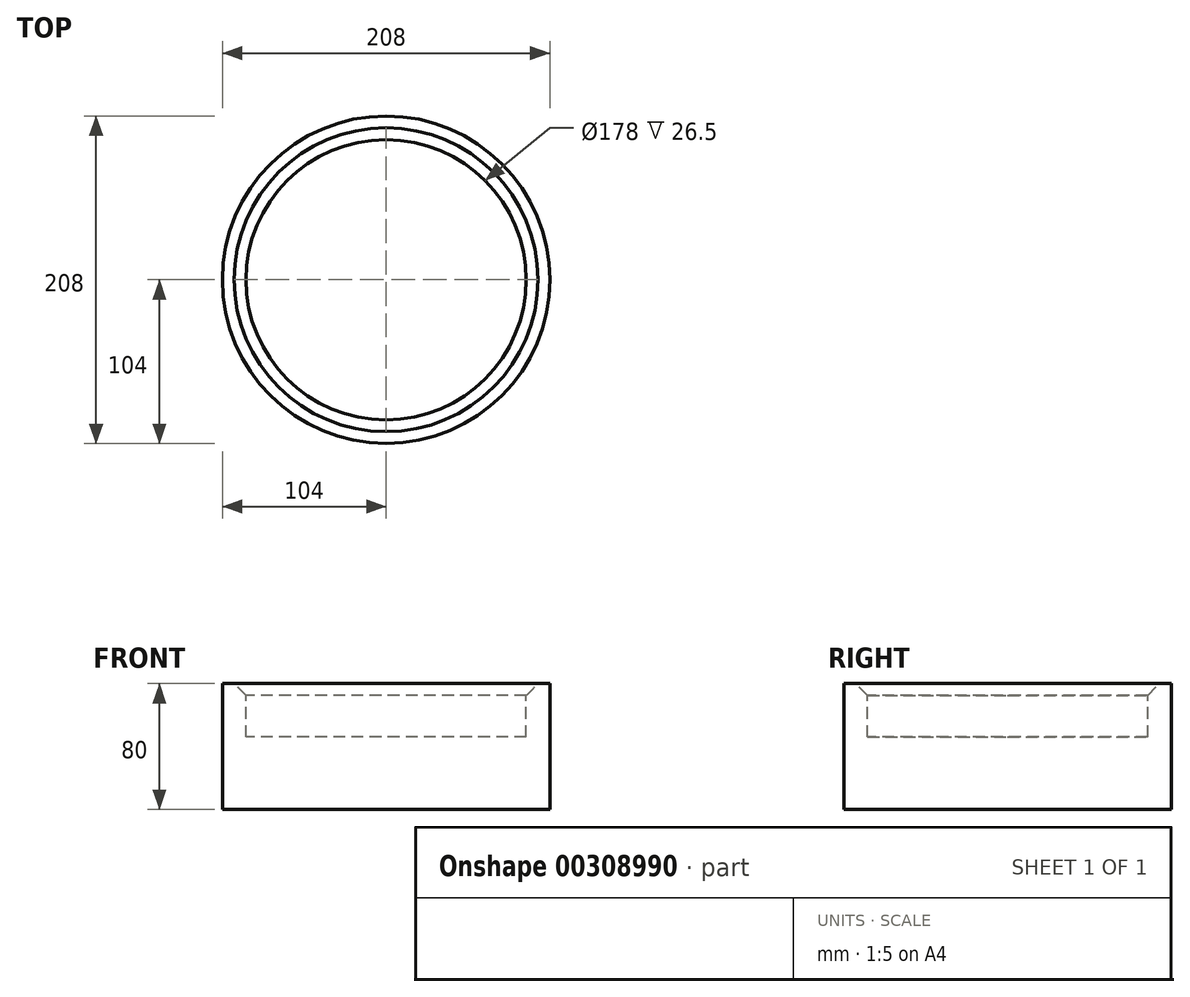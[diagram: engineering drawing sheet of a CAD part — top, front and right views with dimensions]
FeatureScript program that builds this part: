
annotation { "Feature Type Name" : "Feature", "Feature Type Description" : "" }
export const myFeature = defineFeature(function(context is Context, id is Id, definition is map)
    precondition{}
    {
        {
            var Q0;
            Q0=qCreatedBy(makeId("Front.planeOp"),FACE);
            var sketch = newSketch(context, id + "F0", { "sketchPlane" : qUnion([Q0])});
            skLineSegment(sketch, "E0", {"start": v(0, 0) * mm, "end": v(-104, 0) * mm});
            skLineSegment(sketch, "E1", {"start": v(-104, 0) * mm, "end": v(-104, 80) * mm});
            skLineSegment(sketch, "E2", {"start": v(-104, 80) * mm, "end": v(-96.5, 80) * mm});
            skLineSegment(sketch, "E3", {"start": v(-96.5, 80) * mm, "end": v(-89, 72.5) * mm});
            skLineSegment(sketch, "E4", {"start": v(-89, 72.5) * mm, "end": v(-89, 46) * mm});
            skLineSegment(sketch, "E5", {"start": v(-89, 46) * mm, "end": v(0, 46) * mm});
            skLineSegment(sketch, "E6", {"start": v(0, 46) * mm, "end": v(0, 0) * mm});
            skSolve(sketch);
        }
        {
            var Q0;
            Q0=makeQuery(id+"F0.imprint","IMPRINT",FACE,{"disambiguationData":[TD([[makeQuery(id+"F0.imprint","IMPRINT",EDGE,{"derivedFrom":sQuery(id+"F0.wireOp",EDGE,"E0")}),-1.0]])]});
            var Q1;
            Q1=sQuery(id+"F0.wireOp",EDGE,"E6");
            revolve(context, id + "F1", {"entities" : qUnion([Q0]), "axis" : qUnion([Q1]), "revolveType" : RevolveType.FULL});
        }
    });
